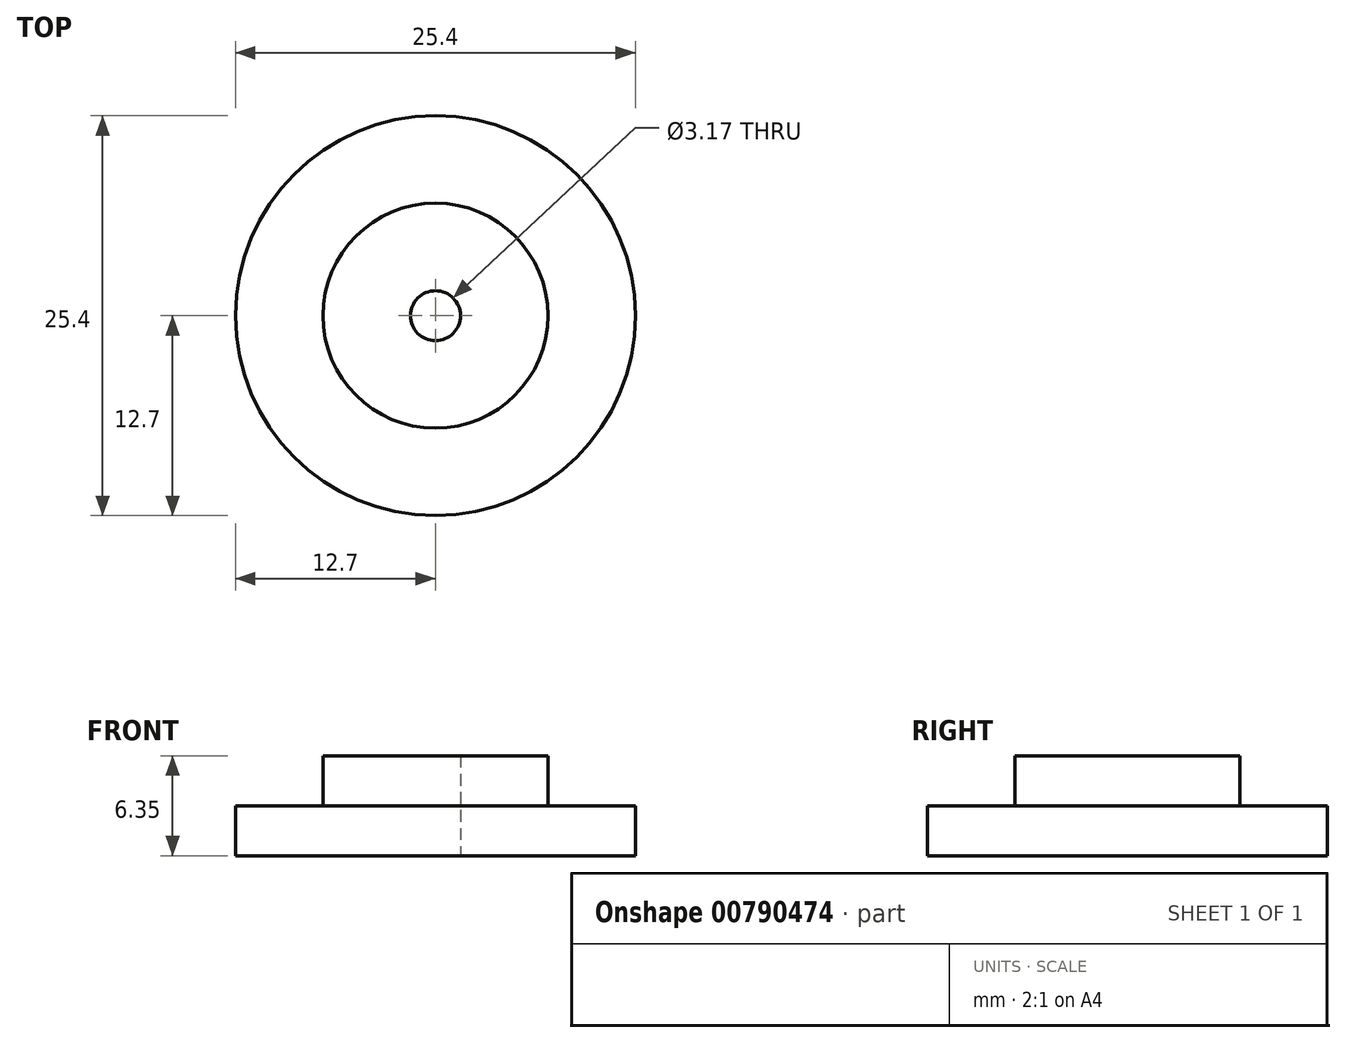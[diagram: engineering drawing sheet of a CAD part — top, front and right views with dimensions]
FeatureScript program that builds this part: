
annotation { "Feature Type Name" : "Feature", "Feature Type Description" : "" }
export const myFeature = defineFeature(function(context is Context, id is Id, definition is map)
    precondition{}
    {
        {
            var Q0;
            Q0=qCreatedBy(makeId("Top.planeOp"),FACE);
            var sketch = newSketch(context, id + "F0", { "sketchPlane" : qUnion([Q0])});
            skCircle(sketch, "E0", {"center": v(0, 0) * mm, "radius": 7.14 * mm});
            skCircle(sketch, "E1", {"center": v(0, 0) * mm, "radius": 12.7 * mm});
            skCircle(sketch, "E2", {"center": v(0, 0) * mm, "radius": 1.59 * mm});
            skSolve(sketch);
        }
        {
            var Q0;
            Q0=makeQuery(id+"F0.imprint","IMPRINT",FACE,{"disambiguationData":[TD([[makeQuery(id+"F0.imprint","IMPRINT",EDGE,{"derivedFrom":sQuery(id+"F0.wireOp",EDGE,"E0")}),-1.0]])]});
            extrude(context, id + "F1", {"entities" : qUnion([Q0]), "depth" : 3.17 * mm, "offsetDistance" : 25.4 * mm});
        }
        {
            var Q0;
            Q0=makeQuery(id+"F0.imprint","IMPRINT",FACE,{"disambiguationData":[TD([[makeQuery(id+"F0.imprint","IMPRINT",EDGE,{"derivedFrom":sQuery(id+"F0.wireOp",EDGE,"E0")}),1.0]])]});
            extrude(context, id + "F2", {"entities" : qUnion([Q0]), "operationType" : NewBodyOperationType.ADD, "depth" : 6.35 * mm, "offsetDistance" : 25.4 * mm});
        }
        {
            var Q0;
            Q0=makeQuery(id+"F0.imprint","IMPRINT",FACE,{"disambiguationData":[TD([[makeQuery(id+"F0.imprint","IMPRINT",EDGE,{"derivedFrom":sQuery(id+"F0.wireOp",EDGE,"E2")}),1.0]])]});
            extrude(context, id + "F3", {"entities" : qUnion([Q0]), "operationType" : NewBodyOperationType.REMOVE, "oppositeDirection" : true, "depth" : 6.35 * mm, "offsetDistance" : 25.4 * mm});
        }
    });
